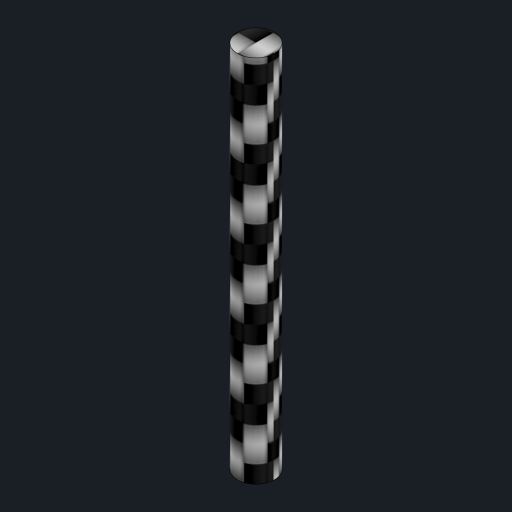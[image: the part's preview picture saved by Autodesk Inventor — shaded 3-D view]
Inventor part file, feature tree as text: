
AUTODESK INVENTOR PART (.ipt)
format: ipt  version: 2023 (Build 270158000, 158)  size: 123,392 bytes
history: native  units: mm
features: other x1, extrude x1, sketch x1
ambient origin geometry x8: Origin, YZ Plane, XZ Plane, XY Plane, X Axis, Y Axis, Z Axis, Center Point
bodies: Body1 (feature_tree)
feature tree (3):
  other  "ソリッド1"
  extrude  "押し出し1"  Depth=2.0mm
  sketch  "スケッチ1"
